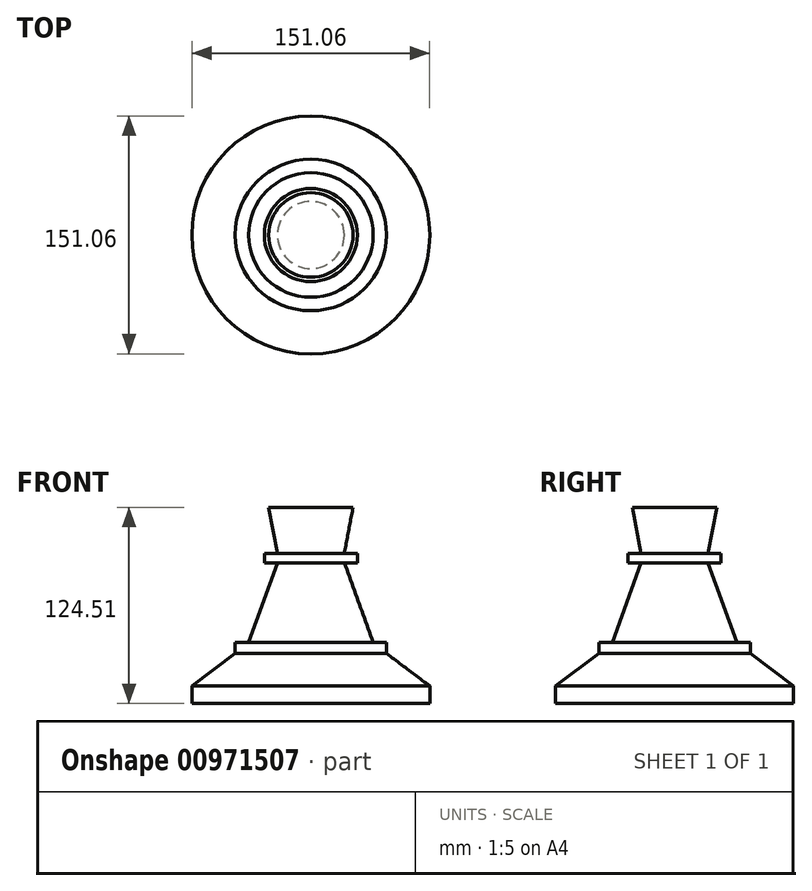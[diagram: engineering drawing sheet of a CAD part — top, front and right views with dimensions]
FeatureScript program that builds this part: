
annotation { "Feature Type Name" : "Feature", "Feature Type Description" : "" }
export const myFeature = defineFeature(function(context is Context, id is Id, definition is map)
    precondition{}
    {
        {
            var Q0;
            Q0=qCreatedBy(makeId("Front.planeOp"),FACE);
            var sketch = newSketch(context, id + "F0", { "sketchPlane" : qUnion([Q0])});
            skLineSegment(sketch, "E0", {"start": v(0, 48.12) * mm, "end": v(-26.8, 48.12) * mm});
            skLineSegment(sketch, "E1", {"start": v(-26.8, 48.12) * mm, "end": v(-21.28, 19) * mm});
            skLineSegment(sketch, "E2", {"start": v(-21.28, 19) * mm, "end": v(-29.56, 19) * mm});
            skLineSegment(sketch, "E3", {"start": v(-29.56, 19) * mm, "end": v(-29.56, 13) * mm});
            skLineSegment(sketch, "E4", {"start": v(-29.56, 13) * mm, "end": v(-21.28, 13) * mm});
            skLineSegment(sketch, "E5", {"start": v(-21.28, 13) * mm, "end": v(-39.55, -37.55) * mm});
            skLineSegment(sketch, "E6", {"start": v(-39.55, -37.55) * mm, "end": v(-48.12, -37.55) * mm});
            skLineSegment(sketch, "E7", {"start": v(-48.12, -37.55) * mm, "end": v(-48.12, -44.7) * mm});
            skLineSegment(sketch, "E8", {"start": v(-48.12, -44.7) * mm, "end": v(-75.53, -65.25) * mm});
            skLineSegment(sketch, "E9", {"start": v(-75.53, -65.25) * mm, "end": v(-75.53, -76.4) * mm});
            skLineSegment(sketch, "E10", {"start": v(-75.53, -76.4) * mm, "end": v(0, -76.4) * mm});
            skLineSegment(sketch, "E11", {"start": v(0, 48.12) * mm, "end": v(0, -76.4) * mm});
            skSolve(sketch);
        }
        {
            var Q0;
            Q0 = qSketchRegion(id + "F0", true);
            var Q1;
            Q1=sQuery(id+"F0.wireOp",EDGE,"E11");
            revolve(context, id + "F1", {"surfaceOperationType" : NewSurfaceOperationType.NEW, "entities" : qUnion([Q0]), "axis" : qUnion([Q1]), "revolveType" : RevolveType.FULL});
        }
    });
